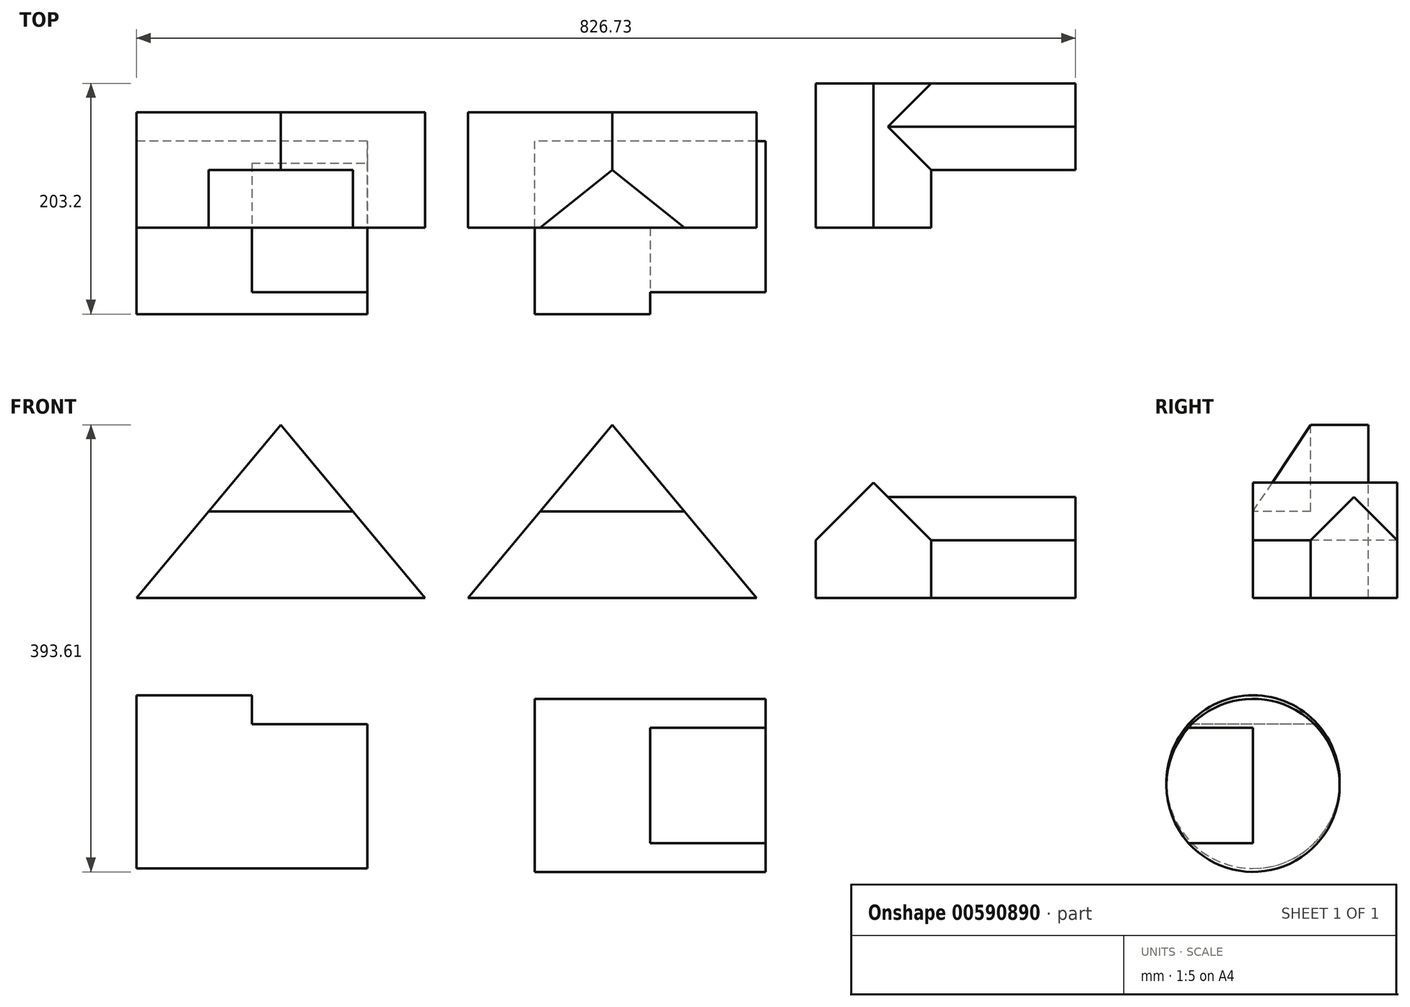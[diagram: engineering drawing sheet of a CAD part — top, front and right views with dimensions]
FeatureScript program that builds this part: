
annotation { "Feature Type Name" : "Feature", "Feature Type Description" : "" }
export const myFeature = defineFeature(function(context is Context, id is Id, definition is map)
    precondition{}
    {
        {
            var Q0;
            Q0=qCreatedBy(makeId("Front.planeOp"),FACE);
            var sketch = newSketch(context, id + "F0", { "sketchPlane" : qUnion([Q0])});
            skLineSegment(sketch, "E0.bottom", {"start": v(0, 0) * mm, "end": v(254, 0) * mm});
            skLineSegment(sketch, "E1", {"start": v(254, 0) * mm, "end": v(127, 152.4) * mm});
            skLineSegment(sketch, "E2", {"start": v(127, 152.4) * mm, "end": v(0, 0) * mm});
            skSolve(sketch);
        }
        {
            var Q0;
            Q0=makeQuery(id+"F0.imprint","IMPRINT",FACE,{"disambiguationData":[TD([[makeQuery(id+"F0.imprint","IMPRINT",EDGE,{"derivedFrom":sQuery(id+"F0.wireOp",EDGE,"E0.bottom")}),1.0]])]});
            extrude(context, id + "F1", {"entities" : qUnion([Q0]), "oppositeDirection" : true, "depth" : 101.6 * mm, "offsetDistance" : 25.4 * mm});
        }
        {
            var Q0;
            Q0=makeQuery(id+"F1.opExtrude","CAP_FACE",FACE,{"disambiguationData":[OSD([sQuery(id+"F0.wireOp",EDGE,"E0.bottom"),sQuery(id+"F0.wireOp",EDGE,"E1"),sQuery(id+"F0.wireOp",EDGE,"E2")])],"isStart":true});
            var sketch = newSketch(context, id + "F2", { "sketchPlane" : qUnion([Q0])});
            skLineSegment(sketch, "E3", {"start": v(127, 76.2) * mm, "end": v(63.5, 76.2) * mm});
            skLineSegment(sketch, "E4", {"start": v(127, 76.2) * mm, "end": v(190.5, 76.2) * mm});
            skSolve(sketch);
        }
        {
            var Q0;
            {var subQ0=sQuery(id+"F2.wireOp",EDGE,"E3");Q0=makeQuery(id+"F2.imprint","IMPRINT",FACE,{"disambiguationData":[TD([[makeQuery(id+"F2.imprint","IMPRINT",EDGE,{"derivedFrom":subQ0}),-1.0]])]});}
            extrude(context, id + "F3", {"entities" : qUnion([Q0]), "operationType" : NewBodyOperationType.REMOVE, "oppositeDirection" : true, "depth" : 50.8 * mm, "offsetDistance" : 25.4 * mm});
        }
        {
            var Q0;
            Q0=qCreatedBy(makeId("Front.planeOp"),FACE);
            var sketch = newSketch(context, id + "F4", { "sketchPlane" : qUnion([Q0])});
            skLineSegment(sketch, "E5.bottom", {"start": v(291.77, 0) * mm, "end": v(545.77, 0) * mm});
            skLineSegment(sketch, "E6", {"start": v(545.77, 0) * mm, "end": v(418.77, 152.4) * mm});
            skLineSegment(sketch, "E7", {"start": v(418.77, 152.4) * mm, "end": v(291.77, 0) * mm});
            skSolve(sketch);
        }
        {
            var Q0;
            Q0=makeQuery(id+"F4.imprint","IMPRINT",FACE,{"disambiguationData":[TD([[makeQuery(id+"F4.imprint","IMPRINT",EDGE,{"derivedFrom":sQuery(id+"F4.wireOp",EDGE,"E5.bottom")}),1.0]])]});
            extrude(context, id + "F5", {"entities" : qUnion([Q0]), "oppositeDirection" : true, "depth" : 101.6 * mm, "offsetDistance" : 25.4 * mm});
        }
        {
            var Q0;
            Q0=qCreatedBy(makeId("Right.planeOp"),FACE);
            cPlane(context, id + "F6", {"entities" : qUnion([Q0]), "cplaneType" : CPlaneType.OFFSET, "offset" : 550.67 * mm, "width" : 152.4 * mm, "height" : 152.4 * mm});
        }
        {
            var Q0;
            Q0=qCreatedBy(id+"F6.planeOp",FACE);
            var sketch = newSketch(context, id + "F7", { "sketchPlane" : qUnion([Q0])});
            skLineSegment(sketch, "E8", {"start": v(0, 76.2) * mm, "end": v(50.8, 152.4) * mm});
            skLineSegment(sketch, "E9", {"start": v(50.8, 152.4) * mm, "end": v(0, 152.4) * mm});
            skLineSegment(sketch, "E10", {"start": v(0, 152.4) * mm, "end": v(0, 76.2) * mm});
            skSolve(sketch);
        }
        {
            var Q0;
            Q0 = qSketchRegion(id + "F7", true);
            extrude(context, id + "F8", {"entities" : qUnion([Q0]), "operationType" : NewBodyOperationType.REMOVE, "oppositeDirection" : true, "depth" : 244.35 * mm, "offsetDistance" : 25.4 * mm});
        }
        {
            var Q0;
            Q0=qCreatedBy(makeId("Front.planeOp"),FACE);
            var sketch = newSketch(context, id + "F9", { "sketchPlane" : qUnion([Q0])});
            skLineSegment(sketch, "E11", {"start": v(598.13, 0) * mm, "end": v(699.73, 0) * mm});
            skLineSegment(sketch, "E12", {"start": v(699.73, 0) * mm, "end": v(699.73, 50.8) * mm});
            skLineSegment(sketch, "E13", {"start": v(598.13, 0) * mm, "end": v(598.13, 50.8) * mm});
            skLineSegment(sketch, "E14", {"start": v(648.93, 101.6) * mm, "end": v(598.13, 50.8) * mm});
            skLineSegment(sketch, "E15", {"start": v(648.93, 101.6) * mm, "end": v(699.73, 50.8) * mm});
            skSolve(sketch);
        }
        {
            var Q0;
            Q0=makeQuery(id+"F9.imprint","IMPRINT",FACE,{"disambiguationData":[TD([[makeQuery(id+"F9.imprint","IMPRINT",EDGE,{"derivedFrom":sQuery(id+"F9.wireOp",EDGE,"E11")}),1.0]])]});
            extrude(context, id + "F10", {"entities" : qUnion([Q0]), "oppositeDirection" : true, "depth" : 127 * mm, "offsetDistance" : 25.4 * mm});
        }
        {
            var Q0;
            Q0=makeQuery(id+"F10.opExtrude","SWEPT_FACE",FACE,{"disambiguationData":[OSD([sQuery(id+"F9.wireOp",EDGE,"E12")])]});
            var sketch = newSketch(context, id + "F11", { "sketchPlane" : qUnion([Q0])});
            skLineSegment(sketch, "E16", {"start": v(127, 0) * mm, "end": v(127, 50.8) * mm});
            skLineSegment(sketch, "E17", {"start": v(127, 0) * mm, "end": v(50.8, 0) * mm});
            skLineSegment(sketch, "E18", {"start": v(50.8, 0) * mm, "end": v(50.8, 50.8) * mm});
            skLineSegment(sketch, "E19", {"start": v(88.9, 88.9) * mm, "end": v(50.8, 50.8) * mm});
            skLineSegment(sketch, "E20", {"start": v(127, 50.8) * mm, "end": v(88.9, 88.9) * mm});
            skSolve(sketch);
        }
        {
            var Q0;
            {var subQ0=sQuery(id+"F11.wireOp",EDGE,"E16");Q0=makeQuery(id+"F11.imprint","IMPRINT",FACE,{"disambiguationData":[TD([[makeQuery(id+"F11.imprint","IMPRINT",EDGE,{"derivedFrom":subQ0}),1.0]])]});}
            var Q1;
            {var subQ0=sQuery(id+"F11.wireOp",EDGE,"E19");Q1=makeQuery(id+"F11.imprint","IMPRINT",FACE,{"disambiguationData":[TD([[makeQuery(id+"F11.imprint","IMPRINT",EDGE,{"derivedFrom":subQ0}),1.0]])]});}
            extrude(context, id + "F12", {"entities" : qUnion([Q0, Q1]), "operationType" : NewBodyOperationType.ADD, "depth" : 127 * mm, "offsetDistance" : 25.4 * mm});
        }
        {
            var Q0;
            {var subQ0=sQuery(id+"F11.wireOp",EDGE,"E19");Q0=makeQuery(id+"F11.imprint","IMPRINT",FACE,{"disambiguationData":[TD([[makeQuery(id+"F11.imprint","IMPRINT",EDGE,{"derivedFrom":subQ0}),1.0]])]});}
            extrude(context, id + "F13", {"entities" : qUnion([Q0]), "operationType" : NewBodyOperationType.ADD, "endBound" : BoundingType.UP_TO_NEXT, "oppositeDirection" : true, "depth" : 25.4 * mm, "offsetDistance" : 25.4 * mm});
        }
        {
            var Q0;
            Q0=qCreatedBy(makeId("Right.planeOp"),FACE);
            var sketch = newSketch(context, id + "F14", { "sketchPlane" : qUnion([Q0])});
            skCircle(sketch, "E21", {"center": v(0, -162) * mm, "radius": 76.2 * mm});
            skSolve(sketch);
        }
        {
            var Q0;
            Q0 = qSketchRegion(id + "F14", true);
            extrude(context, id + "F15", {"entities" : qUnion([Q0]), "depth" : 203.2 * mm, "offsetDistance" : 25.4 * mm});
        }
        {
            var Q0;
            Q0=makeQuery(id+"F15.opExtrude","CAP_FACE",FACE,{"disambiguationData":[OSD([sQuery(id+"F14.wireOp",EDGE,"E21")])],"isStart":false});
            var sketch = newSketch(context, id + "F16", { "sketchPlane" : qUnion([Q0])});
            skLineSegment(sketch, "E22", {"start": v(56.8, -111.2) * mm, "end": v(-56.8, -111.2) * mm});
            skSolve(sketch);
        }
        {
            var Q0;
            Q0 = qSketchRegion(id + "F16", true);
            var Q1;
            {var subQ0=sQuery(id+"F16.wireOp",EDGE,"E22");Q1=makeQuery(id+"F16.imprint","IMPRINT",FACE,{"disambiguationData":[TD([[makeQuery(id+"F16.imprint","IMPRINT",EDGE,{"derivedFrom":subQ0}),-1.0]])]});}
            extrude(context, id + "F17", {"entities" : qUnion([Q0, Q1]), "operationType" : NewBodyOperationType.REMOVE, "oppositeDirection" : true, "depth" : 101.6 * mm, "offsetDistance" : 25.4 * mm});
        }
        {
            var Q0;
            Q0=qCreatedBy(makeId("Right.planeOp"),FACE);
            cPlane(context, id + "F18", {"entities" : qUnion([Q0]), "cplaneType" : CPlaneType.OFFSET, "offset" : 350.52 * mm, "width" : 152.4 * mm, "height" : 152.4 * mm});
        }
        {
            var Q0;
            Q0=qCreatedBy(id+"F18.planeOp",FACE);
            var sketch = newSketch(context, id + "F19", { "sketchPlane" : qUnion([Q0])});
            skCircle(sketch, "E23", {"center": v(0, -165.01) * mm, "radius": 76.2 * mm});
            skLineSegment(sketch, "E24", {"start": v(0, -114.21) * mm, "end": v(-56.8, -114.21) * mm});
            skLineSegment(sketch, "E25", {"start": v(0, -215.81) * mm, "end": v(-56.8, -215.81) * mm});
            skLineSegment(sketch, "E26", {"start": v(0, -114.21) * mm, "end": v(0, -215.81) * mm});
            skSolve(sketch);
        }
        {
            var Q0;
            Q0 = qSketchRegion(id + "F19", true);
            extrude(context, id + "F20", {"entities" : qUnion([Q0]), "depth" : 203.2 * mm, "offsetDistance" : 25.4 * mm});
        }
        {
            var Q0;
            Q0=makeQuery(id+"F20.opExtrude","CAP_FACE",FACE,{"disambiguationData":[OSD([sQuery(id+"F19.wireOp",EDGE,"E23")])],"isStart":false});
            var sketch = newSketch(context, id + "F21", { "sketchPlane" : qUnion([Q0])});
            skLineSegment(sketch, "E27", {"start": v(0, -114.21) * mm, "end": v(-56.8, -114.21) * mm});
            skLineSegment(sketch, "E28", {"start": v(0, -215.81) * mm, "end": v(-56.8, -215.81) * mm});
            skLineSegment(sketch, "E29", {"start": v(0, -114.21) * mm, "end": v(0, -215.81) * mm});
            skSolve(sketch);
        }
        {
            var Q0;
            {var subQ0=sQuery(id+"F21.wireOp",EDGE,"E27");Q0=makeQuery(id+"F21.imprint","IMPRINT",FACE,{"disambiguationData":[TD([[makeQuery(id+"F21.imprint","IMPRINT",EDGE,{"derivedFrom":subQ0}),1.0]])]});}
            extrude(context, id + "F22", {"entities" : qUnion([Q0]), "operationType" : NewBodyOperationType.REMOVE, "oppositeDirection" : true, "depth" : 101.6 * mm, "offsetDistance" : 25.4 * mm});
        }
    });
